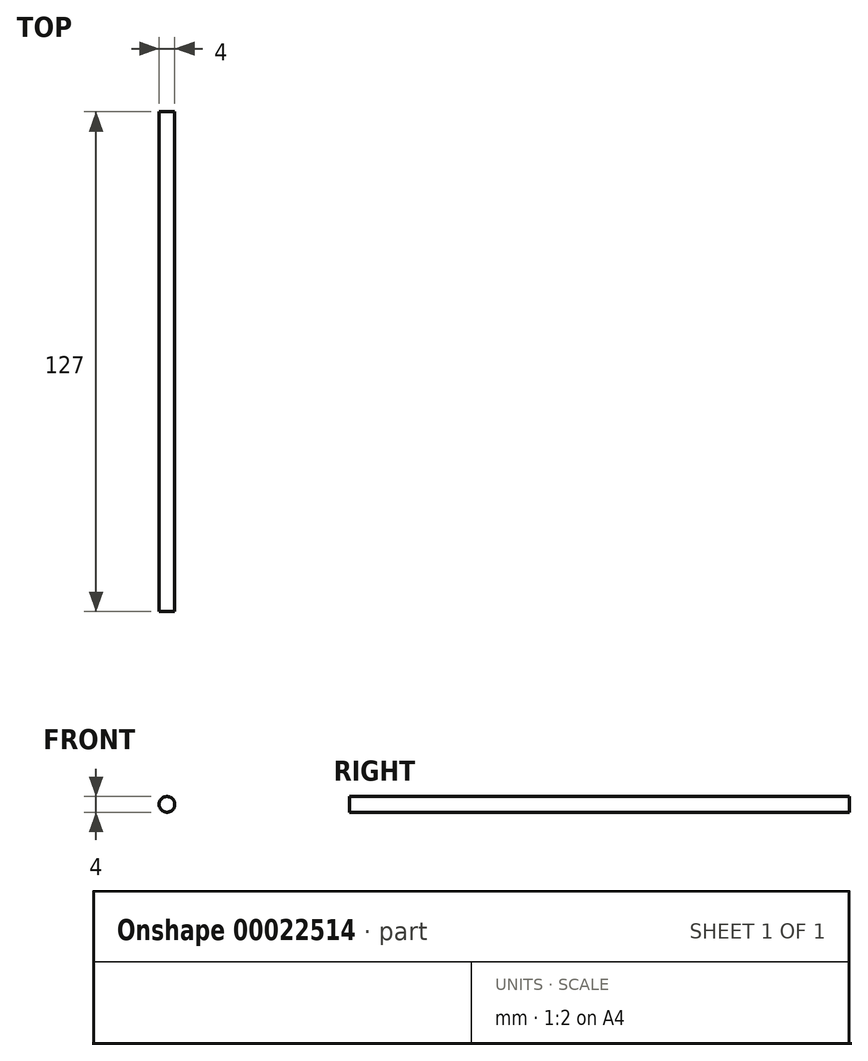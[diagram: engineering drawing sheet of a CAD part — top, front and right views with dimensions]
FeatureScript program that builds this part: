
annotation { "Feature Type Name" : "Feature", "Feature Type Description" : "" }
export const myFeature = defineFeature(function(context is Context, id is Id, definition is map)
    precondition{}
    {
        {
            var Q0;
            Q0=qCreatedBy(makeId("Front.planeOp"),FACE);
            var sketch = newSketch(context, id + "F0", { "sketchPlane" : qUnion([Q0])});
            skCircle(sketch, "E0", {"center": v(-5.03, 19.68) * mm, "radius": 2 * mm});
            skCircle(sketch, "E1", {"center": v(47.84, 14.43) * mm, "radius": 2 * mm});
            skSolve(sketch);
        }
        {
            var Q0;
            Q0=makeQuery(id+"F0.imprint","IMPRINT",FACE,{"disambiguationData":[TD([[makeQuery(id+"F0.imprint","IMPRINT",EDGE,{"derivedFrom":sQuery(id+"F0.wireOp",EDGE,"E0")}),1.0]])]});
            extrude(context, id + "F1", {"entities" : qUnion([Q0]), "depth" : 127 * mm});
        }
        {
            var Q0;
            Q0=sQuery(id+"F0.wireOp",EDGE,"E1");
            extrude(context, id + "F2", {"bodyType" : ToolBodyType.SURFACE, "surfaceEntities" : qUnion([Q0]), "depth" : 127 * mm});
        }
    });
